# Revit family: Storage-Freestanding-Teknion-BSW_Wardrobe_Solid_Doors-R2019
name_source: partatom
category: Furniture
units: mm (PartAtom-declared; Revit-internal decimal feet)

## family parameters
Always vertical = Yes
Cut with Voids When Loaded = No
OmniClass Number = 23.40.20.00
OmniClass Title = General Furniture and Specialties
Room Calculation Point = No
Shared = Yes
Work Plane-Based = No

## types (4) — shared parameters
Assembly Code = E2020200
Manufacturer = Teknion
Manufacturer Fax = 416.661.4586
Part Number = BSWCS
Product Documentation Link = https://www.teknion.com
Product Line = Expansion Casegoods
Product Page URL = https://www.teknion.com
Series = Expansion Casegoods
Sustainability Data = http://www.teknion.com
URL = www.teknion.com
Unit Weight URL = http://www.teknion.com
Warranty = http://www.teknion.com

## per-type parameters (varying)
| type | Description | Model | Pulls | Touch-to-Open |
| Has Pulls, Divided Style | Wardrobe Cabinet – Solid Doors, Pulls Storage Style, Divided Style | BSWCSPD______ | Yes | No |
| Has Pulls, Undivided Style | Wardrobe Cabinet – Solid Doors, Pulls Storage Style, Undivided Style | BSWCSPU______ | Yes | No |
| Has Touch-to-Open, Divided Style | Wardrobe Cabinet – Solid Doors, Touch-to-Open Storage Style, Divided Style | BSWCSTD______ | No | Yes |
| Has Touch-to-Open, Undivided Style | Wardrobe Cabinet – Solid Doors, Touch-to-Open Storage Style, Undivided Style | BSWCSTU______ | No | Yes |

## geometry (parser evidence)
native form markers: Blend x148, Sweep x2
no freeform markers — native parametric forms only
